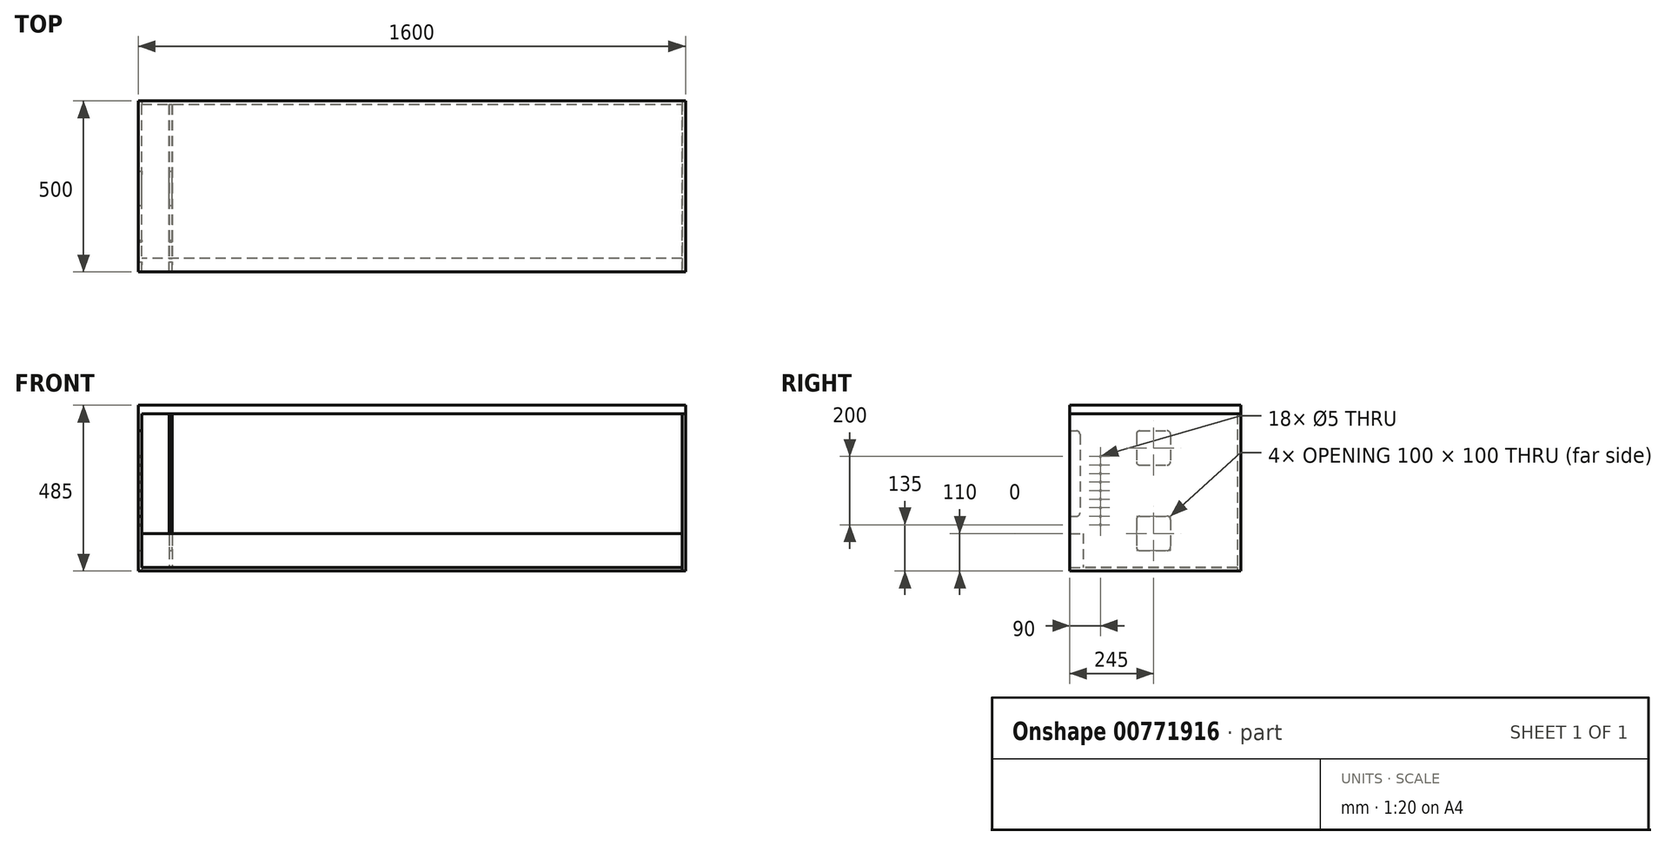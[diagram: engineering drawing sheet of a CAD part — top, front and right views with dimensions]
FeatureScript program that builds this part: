
annotation { "Feature Type Name" : "Feature", "Feature Type Description" : "" }
export const myFeature = defineFeature(function(context is Context, id is Id, definition is map)
    precondition{}
    {
        {
            var Q0;
            Q0=qCreatedBy(makeId("Top.planeOp"),FACE);
            var sketch = newSketch(context, id + "F0", { "sketchPlane" : qUnion([Q0])});
            skLineSegment(sketch, "E0.bottom", {"start": v(0, 0) * mm, "end": v(1600, 0) * mm});
            skLineSegment(sketch, "E0.top", {"start": v(0, 500) * mm, "end": v(1600, 500) * mm});
            skLineSegment(sketch, "E0.left", {"start": v(0, 0) * mm, "end": v(0, 500) * mm});
            skLineSegment(sketch, "E0.right", {"start": v(1600, 0) * mm, "end": v(1600, 500) * mm});
            skSolve(sketch);
        }
        {
            var Q0;
            Q0=makeQuery(id+"F0.imprint","IMPRINT",FACE,{"disambiguationData":[TD([[makeQuery(id+"F0.imprint","IMPRINT",EDGE,{"derivedFrom":sQuery(id+"F0.wireOp",EDGE,"E0.bottom")}),1.0]])]});
            extrude(context, id + "F1", {"entities" : qUnion([Q0]), "depth" : 25 * mm, "offsetDistance" : 25 * mm});
        }
        {
            var Q0;
            Q0=makeQuery(id+"F0.imprint","IMPRINT",FACE,{"disambiguationData":[TD([[makeQuery(id+"F0.imprint","IMPRINT",EDGE,{"derivedFrom":sQuery(id+"F0.wireOp",EDGE,"E0.bottom")}),1.0]])]});
            cPlane(context, id + "F2", {"entities" : qUnion([Q0]), "cplaneType" : CPlaneType.OFFSET, "offset" : 460 * mm, "oppositeDirection" : true, "width" : 150 * mm, "height" : 150 * mm});
        }
        {
            var Q0;
            Q0=qCreatedBy(id+"F2.planeOp",FACE);
            var sketch = newSketch(context, id + "F3", { "sketchPlane" : qUnion([Q0])});
            skLineSegment(sketch, "E1.bottom", {"start": v(10, 0) * mm, "end": v(1590, 0) * mm});
            skLineSegment(sketch, "E1.top", {"start": v(10, 490) * mm, "end": v(1590, 490) * mm});
            skLineSegment(sketch, "E1.left", {"start": v(10, 0) * mm, "end": v(10, 490) * mm});
            skLineSegment(sketch, "E1.right", {"start": v(1590, 0) * mm, "end": v(1590, 490) * mm});
            skSolve(sketch);
        }
        {
            var Q0;
            Q0=makeQuery(id+"F3.imprint","IMPRINT",FACE,{"disambiguationData":[TD([[makeQuery(id+"F3.imprint","IMPRINT",EDGE,{"derivedFrom":sQuery(id+"F3.wireOp",EDGE,"E1.bottom")}),1.0]])]});
            extrude(context, id + "F4", {"entities" : qUnion([Q0]), "depth" : 10 * mm, "offsetDistance" : 25 * mm});
        }
        {
            var Q0;
            Q0=makeQuery(id+"F0.imprint","IMPRINT",FACE,{"disambiguationData":[TD([[makeQuery(id+"F0.imprint","IMPRINT",EDGE,{"derivedFrom":sQuery(id+"F0.wireOp",EDGE,"E0.bottom")}),1.0]])]});
            var sketch = newSketch(context, id + "F5", { "sketchPlane" : qUnion([Q0])});
            skLineSegment(sketch, "E2.bottom", {"start": v(0, 0) * mm, "end": v(10, 0) * mm});
            skLineSegment(sketch, "E2.top", {"start": v(0, 500) * mm, "end": v(10, 500) * mm});
            skLineSegment(sketch, "E2.left", {"start": v(0, 0) * mm, "end": v(0, 500) * mm});
            skLineSegment(sketch, "E2.right", {"start": v(10, 0) * mm, "end": v(10, 500) * mm});
            skSolve(sketch);
        }
        {
            var Q0;
            Q0=qSketchRegion(id+"F5",true);
            var Q1;
            Q1=makeQuery(id+"F4.opExtrude","CAP_FACE",FACE,{"disambiguationData":[OSD([sQuery(id+"F3.wireOp",EDGE,"E1.bottom"),sQuery(id+"F3.wireOp",EDGE,"E1.top"),sQuery(id+"F3.wireOp",EDGE,"E1.left"),sQuery(id+"F3.wireOp",EDGE,"E1.right")])],"isStart":true});
            extrude(context, id + "F6", {"entities" : qUnion([Q0]), "operationType" : NewBodyOperationType.ADD, "endBound" : BoundingType.UP_TO_SURFACE, "oppositeDirection" : true, "depth" : 25 * mm, "endBoundEntityFace" : qUnion([Q1]), "offsetDistance" : 25 * mm});
        }
        {
            var Q0;
            Q0=makeQuery(id+"F0.imprint","IMPRINT",FACE,{"disambiguationData":[TD([[makeQuery(id+"F0.imprint","IMPRINT",EDGE,{"derivedFrom":sQuery(id+"F0.wireOp",EDGE,"E0.bottom")}),1.0]])]});
            var sketch = newSketch(context, id + "F7", { "sketchPlane" : qUnion([Q0])});
            skLineSegment(sketch, "E3.bottom", {"start": v(1600, 0) * mm, "end": v(1590, 0) * mm});
            skLineSegment(sketch, "E3.top", {"start": v(1600, 500) * mm, "end": v(1590, 500) * mm});
            skLineSegment(sketch, "E3.left", {"start": v(1600, 0) * mm, "end": v(1600, 500) * mm});
            skLineSegment(sketch, "E3.right", {"start": v(1590, 0) * mm, "end": v(1590, 500) * mm});
            skSolve(sketch);
        }
        {
            var Q0;
            Q0=makeQuery(id+"F7.imprint","IMPRINT",FACE,{"disambiguationData":[TD([[makeQuery(id+"F7.imprint","IMPRINT",EDGE,{"derivedFrom":sQuery(id+"F7.wireOp",EDGE,"E3.bottom")}),1.0]])]});
            var Q1;
            Q1=makeQuery(id+"F4.opExtrude","CAP_FACE",FACE,{"disambiguationData":[OSD([sQuery(id+"F3.wireOp",EDGE,"E1.bottom"),sQuery(id+"F3.wireOp",EDGE,"E1.top"),sQuery(id+"F3.wireOp",EDGE,"E1.left"),sQuery(id+"F3.wireOp",EDGE,"E1.right")])],"isStart":true});
            extrude(context, id + "F8", {"entities" : qUnion([Q0]), "endBound" : BoundingType.UP_TO_SURFACE, "oppositeDirection" : true, "depth" : 25 * mm, "endBoundEntityFace" : qUnion([Q1]), "offsetDistance" : 25 * mm});
        }
        {
            var Q0;
            Q0=makeQuery(id+"F6.opExtrude","SWEPT_FACE",FACE,{"disambiguationData":[OSD([sQuery(id+"F5.wireOp",EDGE,"E2.right")])]});
            var sketch = newSketch(context, id + "F9", { "sketchPlane" : qUnion([Q0])});
            skLineSegment(sketch, "E4.bottom", {"start": v(0, -350) * mm, "end": v(40, -350) * mm});
            skLineSegment(sketch, "E4.top", {"start": v(0, -450) * mm, "end": v(40, -450) * mm});
            skLineSegment(sketch, "E4.left", {"start": v(0, -350) * mm, "end": v(0, -450) * mm});
            skLineSegment(sketch, "E4.right", {"start": v(40, -350) * mm, "end": v(40, -450) * mm});
            skSolve(sketch);
        }
        {
            var Q0;
            Q0=makeQuery(id+"F9.imprint","IMPRINT",FACE,{"disambiguationData":[TD([[makeQuery(id+"F9.imprint","IMPRINT",EDGE,{"derivedFrom":sQuery(id+"F9.wireOp",EDGE,"E4.bottom")}),-1.0]])]});
            extrude(context, id + "F10", {"entities" : qUnion([Q0]), "endBound" : BoundingType.UP_TO_NEXT, "depth" : 25 * mm, "offsetDistance" : 25 * mm});
        }
        {
            var Q0;
            Q0=makeQuery(id+"F4.opExtrude","CAP_FACE",FACE,{"disambiguationData":[OSD([sQuery(id+"F3.wireOp",EDGE,"E1.bottom"),sQuery(id+"F3.wireOp",EDGE,"E1.top"),sQuery(id+"F3.wireOp",EDGE,"E1.left"),sQuery(id+"F3.wireOp",EDGE,"E1.right")])],"isStart":false});
            var sketch = newSketch(context, id + "F11", { "sketchPlane" : qUnion([Q0])});
            skLineSegment(sketch, "E5.bottom", {"start": v(100, 490) * mm, "end": v(90, 490) * mm});
            skLineSegment(sketch, "E5.top", {"start": v(100, 40) * mm, "end": v(90, 40) * mm});
            skLineSegment(sketch, "E5.left", {"start": v(100, 490) * mm, "end": v(100, 40) * mm});
            skLineSegment(sketch, "E5.right", {"start": v(90, 490) * mm, "end": v(90, 40) * mm});
            skSolve(sketch);
        }
        {
            var Q0;
            Q0=makeQuery(id+"F11.imprint","IMPRINT",FACE,{"disambiguationData":[TD([[makeQuery(id+"F11.imprint","IMPRINT",EDGE,{"derivedFrom":sQuery(id+"F11.wireOp",EDGE,"E5.bottom")}),-1.0]])]});
            extrude(context, id + "F12", {"entities" : qUnion([Q0]), "endBound" : BoundingType.UP_TO_NEXT, "depth" : 25 * mm, "offsetDistance" : 25 * mm});
        }
        {
            var Q0;
            Q0=makeQuery(id+"F12.opExtrude","SWEPT_FACE",FACE,{"disambiguationData":[OSD([sQuery(id+"F11.wireOp",EDGE,"E5.top")])]});
            var sketch = newSketch(context, id + "F13", { "sketchPlane" : qUnion([Q0])});
            skLineSegment(sketch, "E6.bottom", {"start": v(90, 0) * mm, "end": v(100, 0) * mm});
            skLineSegment(sketch, "E6.top", {"start": v(90, -350) * mm, "end": v(100, -350) * mm});
            skLineSegment(sketch, "E6.left", {"start": v(90, 0) * mm, "end": v(90, -350) * mm});
            skLineSegment(sketch, "E6.right", {"start": v(100, 0) * mm, "end": v(100, -350) * mm});
            skSolve(sketch);
        }
        {
            var Q0;
            Q0=makeQuery(id+"F13.imprint","IMPRINT",FACE,{"disambiguationData":[TD([[makeQuery(id+"F13.imprint","IMPRINT",EDGE,{"derivedFrom":sQuery(id+"F13.wireOp",EDGE,"E6.bottom")}),1.0]])]});
            var Q1;
            Q1=makeQuery(id+"F10.opExtrude","SWEPT_FACE",FACE,{"disambiguationData":[OSD([sQuery(id+"F9.wireOp",EDGE,"E4.left")])]});
            extrude(context, id + "F14", {"entities" : qUnion([Q0]), "endBound" : BoundingType.UP_TO_SURFACE, "depth" : 25 * mm, "endBoundEntityFace" : qUnion([Q1]), "offsetDistance" : 25 * mm});
        }
        {
            var Q0;
            Q0=makeQuery(id+"F14.opExtrude","SWEPT_BODY",BODY,{"disambiguationData":[OSD([sQuery(id+"F13.wireOp",EDGE,"E6.bottom"),sQuery(id+"F13.wireOp",EDGE,"E6.top"),sQuery(id+"F13.wireOp",EDGE,"E6.left"),sQuery(id+"F13.wireOp",EDGE,"E6.right")])]});
            var Q1;
            Q1=makeQuery(id+"F12.opExtrude","SWEPT_BODY",BODY,{"disambiguationData":[OSD([sQuery(id+"F11.wireOp",EDGE,"E5.bottom"),sQuery(id+"F11.wireOp",EDGE,"E5.top"),sQuery(id+"F11.wireOp",EDGE,"E5.left"),sQuery(id+"F11.wireOp",EDGE,"E5.right")])]});
            booleanBodies(context, id + "F15", {"operationType" : BooleanOperationType.UNION, "tools" : qUnion([Q0, Q1])});
        }
        {
            var Q0;
            Q0=makeQuery(id+"F15.opBoolean","MERGE",FACE,{"derivedFrom":[makeQuery(id+"F12.opExtrude","SWEPT_FACE",FACE,{"disambiguationData":[OSD([sQuery(id+"F11.wireOp",EDGE,"E5.left")])]}),makeQuery(id+"F14.opExtrude","SWEPT_FACE",FACE,{"disambiguationData":[OSD([sQuery(id+"F13.wireOp",EDGE,"E6.right")])]})]});
            var sketch = newSketch(context, id + "F16", { "sketchPlane" : qUnion([Q0])});
            skLineSegment(sketch, "E7.bottom", {"start": v(0, -50) * mm, "end": v(30, -50) * mm});
            skLineSegment(sketch, "E7.top", {"start": v(0, -300) * mm, "end": v(30, -300) * mm});
            skLineSegment(sketch, "E7.left", {"start": v(0, -50) * mm, "end": v(0, -300) * mm});
            skLineSegment(sketch, "E7.right", {"start": v(30, -50) * mm, "end": v(30, -300) * mm});
            skSolve(sketch);
        }
        {
            var Q0;
            Q0=makeQuery(id+"F16.imprint","IMPRINT",FACE,{"disambiguationData":[TD([[makeQuery(id+"F16.imprint","IMPRINT",EDGE,{"derivedFrom":sQuery(id+"F16.wireOp",EDGE,"E7.bottom")}),-1.0]])]});
            extrude(context, id + "F17", {"entities" : qUnion([Q0]), "operationType" : NewBodyOperationType.REMOVE, "endBound" : BoundingType.THROUGH_ALL, "oppositeDirection" : true, "depth" : 25 * mm, "offsetDistance" : 25 * mm});
        }
        {
            var Q0;
            Q0=makeQuery(id+"F17.boolean.opBoolean","COPY",EDGE,{"derivedFrom":makeQuery(id+"F17.opExtrude","SWEPT_EDGE",EDGE,{"disambiguationData":[OSD([sQuery(id+"F16.wireOp",EDGE,"E7.bottom"),sQuery(id+"F16.wireOp",EDGE,"E7.right")])]})});
            var Q1;
            Q1=makeQuery(id+"F17.boolean.opBoolean","COPY",EDGE,{"derivedFrom":makeQuery(id+"F17.opExtrude","SWEPT_EDGE",EDGE,{"disambiguationData":[OSD([sQuery(id+"F16.wireOp",EDGE,"E7.top"),sQuery(id+"F16.wireOp",EDGE,"E7.right")])]})});
            fillet(context, id + "F18", {"entities" : qUnion([Q0, Q1]), "radius" : 10 * mm, "tangentPropagation" : true, "allowEdgeOverflow" : false});
        }
        {
            var Q0;
            Q0=makeQuery(id+"F15.opBoolean","MERGE",FACE,{"derivedFrom":[makeQuery(id+"F12.opExtrude","SWEPT_FACE",FACE,{"disambiguationData":[OSD([sQuery(id+"F11.wireOp",EDGE,"E5.left")])]}),makeQuery(id+"F14.opExtrude","SWEPT_FACE",FACE,{"disambiguationData":[OSD([sQuery(id+"F13.wireOp",EDGE,"E6.right")])]})]});
            var sketch = newSketch(context, id + "F19", { "sketchPlane" : qUnion([Q0])});
            skLineSegment(sketch, "E8.bottom", {"start": v(205, -300) * mm, "end": v(285, -300) * mm});
            skLineSegment(sketch, "E8.top", {"start": v(205, -400) * mm, "end": v(285, -400) * mm});
            skLineSegment(sketch, "E8.left", {"start": v(195, -310) * mm, "end": v(195, -390) * mm});
            skLineSegment(sketch, "E8.right", {"start": v(295, -310) * mm, "end": v(295, -390) * mm});
            skPoint(sketch, "E9.visualSharp", {"position": v(195, -300) * mm});
            skArc(sketch, "E9.filletArc", {"start": v(205, -300) * mm, "mid": v(197.93, -302.93) * mm, "end": v(195, -310) * mm});
            skPoint(sketch, "E10.visualSharp", {"position": v(295, -300) * mm});
            skArc(sketch, "E10.filletArc", {"start": v(295, -310) * mm, "mid": v(292.07, -302.93) * mm, "end": v(285, -300) * mm});
            skPoint(sketch, "E11.visualSharp", {"position": v(295, -400) * mm});
            skArc(sketch, "E11.filletArc", {"start": v(285, -400) * mm, "mid": v(292.07, -397.07) * mm, "end": v(295, -390) * mm});
            skPoint(sketch, "E12.visualSharp", {"position": v(195, -400) * mm});
            skArc(sketch, "E12.filletArc", {"start": v(195, -390) * mm, "mid": v(197.93, -397.07) * mm, "end": v(205, -400) * mm});
            skLineSegment(sketch, "E13.bottom", {"start": v(205, -50) * mm, "end": v(285, -50) * mm});
            skLineSegment(sketch, "E13.top", {"start": v(205, -150) * mm, "end": v(285, -150) * mm});
            skLineSegment(sketch, "E13.left", {"start": v(195, -60) * mm, "end": v(195, -140) * mm});
            skLineSegment(sketch, "E13.right", {"start": v(295, -60) * mm, "end": v(295, -140) * mm});
            skPoint(sketch, "E14.visualSharp", {"position": v(195, -50) * mm});
            skArc(sketch, "E14.filletArc", {"start": v(205, -50) * mm, "mid": v(197.93, -52.93) * mm, "end": v(195, -60) * mm});
            skPoint(sketch, "E15.visualSharp", {"position": v(295, -50) * mm});
            skArc(sketch, "E15.filletArc", {"start": v(295, -60) * mm, "mid": v(292.07, -52.93) * mm, "end": v(285, -50) * mm});
            skPoint(sketch, "E16.visualSharp", {"position": v(295, -150) * mm});
            skArc(sketch, "E16.filletArc", {"start": v(285, -150) * mm, "mid": v(292.07, -147.07) * mm, "end": v(295, -140) * mm});
            skPoint(sketch, "E17.visualSharp", {"position": v(195, -150) * mm});
            skArc(sketch, "E17.filletArc", {"start": v(195, -140) * mm, "mid": v(197.93, -147.07) * mm, "end": v(205, -150) * mm});
            skSolve(sketch);
        }
        {
            var Q0;
            Q0=makeQuery(id+"F19.imprint","IMPRINT",FACE,{"disambiguationData":[TD([[makeQuery(id+"F19.imprint","IMPRINT",EDGE,{"derivedFrom":sQuery(id+"F19.wireOp",EDGE,"E13.bottom")}),-1.0]])]});
            var Q1;
            Q1=makeQuery(id+"F19.imprint","IMPRINT",FACE,{"disambiguationData":[TD([[makeQuery(id+"F19.imprint","IMPRINT",EDGE,{"derivedFrom":sQuery(id+"F19.wireOp",EDGE,"E8.bottom")}),-1.0]])]});
            extrude(context, id + "F20", {"entities" : qUnion([Q0, Q1]), "operationType" : NewBodyOperationType.REMOVE, "endBound" : BoundingType.THROUGH_ALL, "oppositeDirection" : true, "depth" : 25 * mm, "offsetDistance" : 25 * mm});
        }
        {
            var Q0;
            Q0=makeQuery(id+"F15.opBoolean","MERGE",FACE,{"derivedFrom":[makeQuery(id+"F12.opExtrude","SWEPT_FACE",FACE,{"disambiguationData":[OSD([sQuery(id+"F11.wireOp",EDGE,"E5.left")])]}),makeQuery(id+"F14.opExtrude","SWEPT_FACE",FACE,{"disambiguationData":[OSD([sQuery(id+"F13.wireOp",EDGE,"E6.right")])]})]});
            var sketch = newSketch(context, id + "F21", { "sketchPlane" : qUnion([Q0])});
            skCircle(sketch, "E18", {"center": v(90, -325) * mm, "radius": 2.5 * mm});
            skCircle(sketch, "E19", {"center": v(90, -300) * mm, "radius": 2.5 * mm});
            skCircle(sketch, "E20", {"center": v(90, -275) * mm, "radius": 2.5 * mm});
            skCircle(sketch, "E21", {"center": v(90, -250) * mm, "radius": 2.5 * mm});
            skCircle(sketch, "E22", {"center": v(90, -225) * mm, "radius": 2.5 * mm});
            skCircle(sketch, "E23", {"center": v(90, -200) * mm, "radius": 2.5 * mm});
            skCircle(sketch, "E24", {"center": v(90, -175) * mm, "radius": 2.5 * mm});
            skCircle(sketch, "E25", {"center": v(90, -150) * mm, "radius": 2.5 * mm});
            skCircle(sketch, "E26", {"center": v(90, -125) * mm, "radius": 2.5 * mm});
            skSolve(sketch);
        }
        {
            var Q0;
            Q0=makeQuery(id+"F21.imprint","IMPRINT",FACE,{"disambiguationData":[TD([[makeQuery(id+"F21.imprint","IMPRINT",EDGE,{"derivedFrom":sQuery(id+"F21.wireOp",EDGE,"E18")}),1.0]])]});
            var Q1;
            Q1=makeQuery(id+"F21.imprint","IMPRINT",FACE,{"disambiguationData":[TD([[makeQuery(id+"F21.imprint","IMPRINT",EDGE,{"derivedFrom":sQuery(id+"F21.wireOp",EDGE,"E19")}),1.0]])]});
            var Q2;
            Q2=makeQuery(id+"F21.imprint","IMPRINT",FACE,{"disambiguationData":[TD([[makeQuery(id+"F21.imprint","IMPRINT",EDGE,{"derivedFrom":sQuery(id+"F21.wireOp",EDGE,"E20")}),1.0]])]});
            var Q3;
            Q3=makeQuery(id+"F21.imprint","IMPRINT",FACE,{"disambiguationData":[TD([[makeQuery(id+"F21.imprint","IMPRINT",EDGE,{"derivedFrom":sQuery(id+"F21.wireOp",EDGE,"E21")}),1.0]])]});
            var Q4;
            Q4=makeQuery(id+"F21.imprint","IMPRINT",FACE,{"disambiguationData":[TD([[makeQuery(id+"F21.imprint","IMPRINT",EDGE,{"derivedFrom":sQuery(id+"F21.wireOp",EDGE,"E22")}),1.0]])]});
            var Q5;
            Q5=makeQuery(id+"F21.imprint","IMPRINT",FACE,{"disambiguationData":[TD([[makeQuery(id+"F21.imprint","IMPRINT",EDGE,{"derivedFrom":sQuery(id+"F21.wireOp",EDGE,"E23")}),1.0]])]});
            var Q6;
            Q6=makeQuery(id+"F21.imprint","IMPRINT",FACE,{"disambiguationData":[TD([[makeQuery(id+"F21.imprint","IMPRINT",EDGE,{"derivedFrom":sQuery(id+"F21.wireOp",EDGE,"E24")}),1.0]])]});
            var Q7;
            Q7=makeQuery(id+"F21.imprint","IMPRINT",FACE,{"disambiguationData":[TD([[makeQuery(id+"F21.imprint","IMPRINT",EDGE,{"derivedFrom":sQuery(id+"F21.wireOp",EDGE,"E25")}),1.0]])]});
            var Q8;
            Q8=makeQuery(id+"F21.imprint","IMPRINT",FACE,{"disambiguationData":[TD([[makeQuery(id+"F21.imprint","IMPRINT",EDGE,{"derivedFrom":sQuery(id+"F21.wireOp",EDGE,"E26")}),1.0]])]});
            extrude(context, id + "F22", {"entities" : qUnion([Q0, Q1, Q2, Q3, Q4, Q5, Q6, Q7, Q8]), "operationType" : NewBodyOperationType.REMOVE, "endBound" : BoundingType.THROUGH_ALL, "oppositeDirection" : true, "depth" : 25 * mm, "offsetDistance" : 25 * mm});
        }
    });
